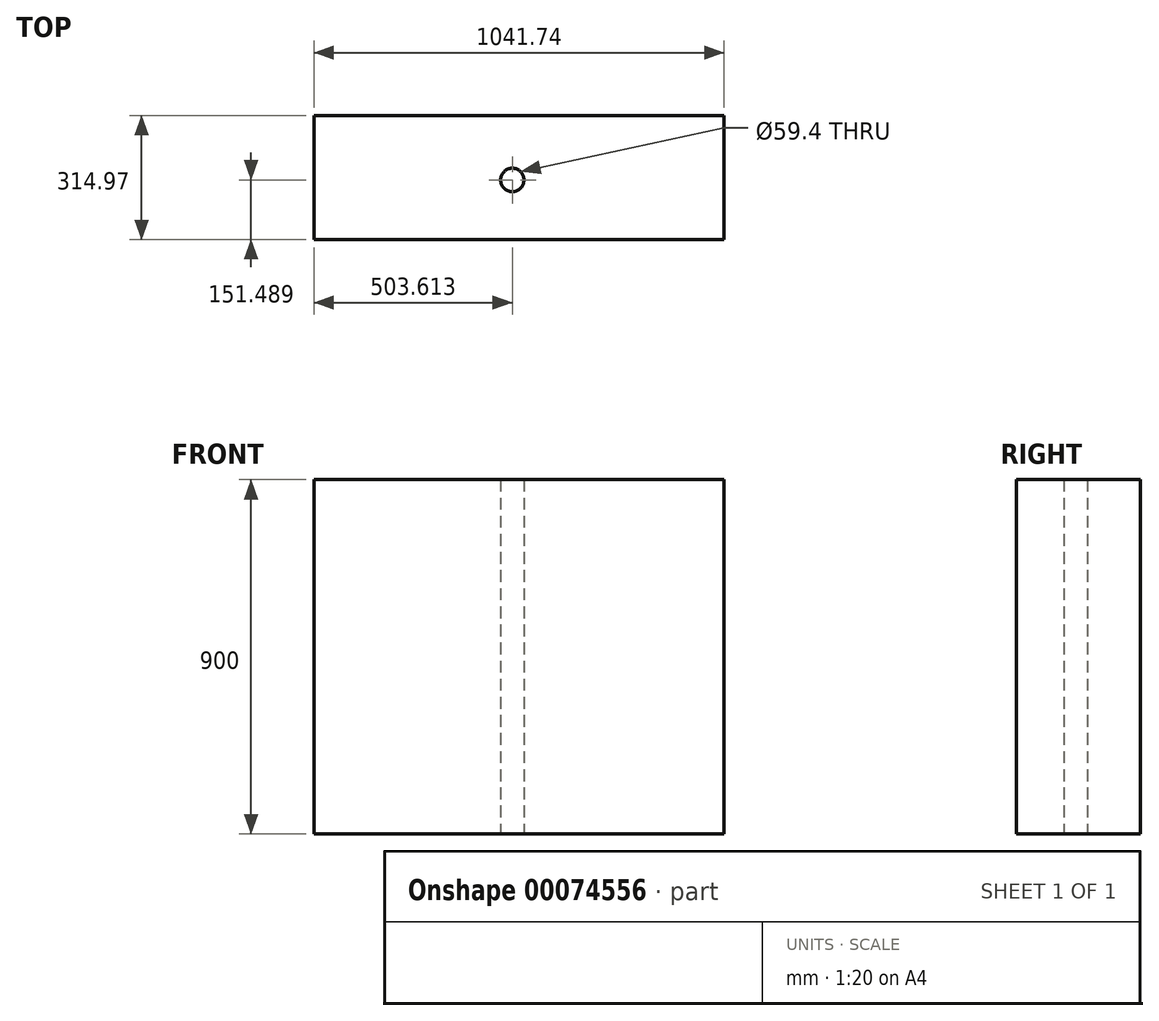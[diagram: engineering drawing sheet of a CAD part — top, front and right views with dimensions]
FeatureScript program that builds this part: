
annotation { "Feature Type Name" : "Feature", "Feature Type Description" : "" }
export const myFeature = defineFeature(function(context is Context, id is Id, definition is map)
    precondition{}
    {
        {
            var Q0;
            Q0=qCreatedBy(makeId("Top.planeOp"),FACE);
            var sketch = newSketch(context, id + "F0", { "sketchPlane" : qUnion([Q0])});
            skLineSegment(sketch, "E0.bottom", {"start": v(-1041.74, 57.1) * mm, "end": v(0, 57.1) * mm});
            skLineSegment(sketch, "E0.top", {"start": v(-1041.74, -257.87) * mm, "end": v(0, -257.87) * mm});
            skLineSegment(sketch, "E0.left", {"start": v(-1041.74, 57.1) * mm, "end": v(-1041.74, -257.87) * mm});
            skLineSegment(sketch, "E0.right", {"start": v(0, 57.1) * mm, "end": v(0, -257.87) * mm});
            skCircle(sketch, "E1", {"center": v(-538.13, -106.38) * mm, "radius": 29.7 * mm});
            skSolve(sketch);
        }
        {
            var Q0;
            Q0=makeQuery(id+"F0.imprint","IMPRINT",FACE,{"disambiguationData":[TD([[makeQuery(id+"F0.imprint","IMPRINT",EDGE,{"derivedFrom":sQuery(id+"F0.wireOp",EDGE,"E0.bottom")}),-1.0]])]});
            extrude(context, id + "F1", {"entities" : qUnion([Q0]), "depth" : 900 * mm});
        }
    });
